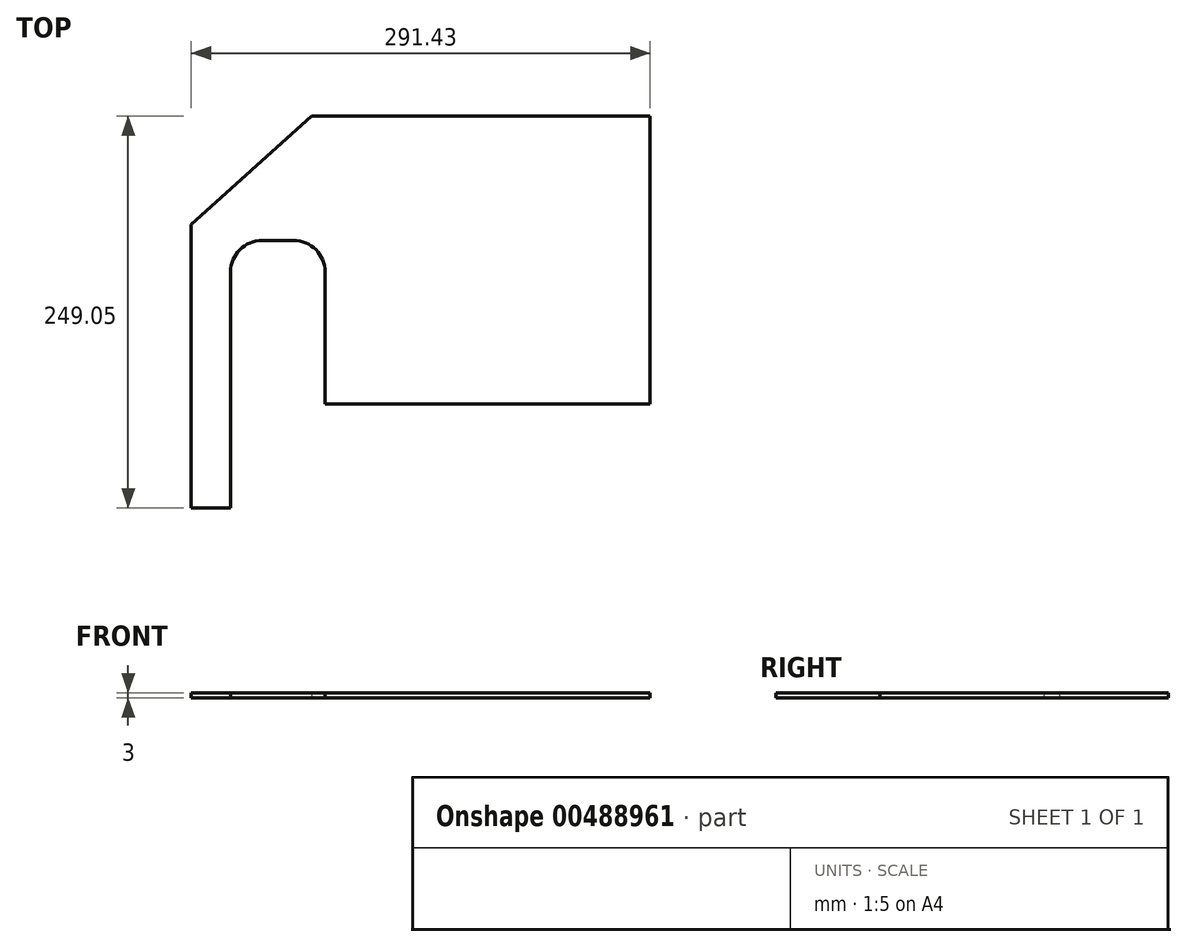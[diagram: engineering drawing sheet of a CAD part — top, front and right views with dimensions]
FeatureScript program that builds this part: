
annotation { "Feature Type Name" : "Feature", "Feature Type Description" : "" }
export const myFeature = defineFeature(function(context is Context, id is Id, definition is map)
    precondition{}
    {
        {
            var Q0;
            Q0=qCreatedBy(makeId("Top.planeOp"),FACE);
            var sketch = newSketch(context, id + "F0", { "sketchPlane" : qUnion([Q0])});
            skLineSegment(sketch, "E0", {"start": v(-110.58, 54.55) * mm, "end": v(-110.58, -125.45) * mm});
            skLineSegment(sketch, "E1", {"start": v(-110.58, -125.45) * mm, "end": v(-85.58, -125.45) * mm});
            skLineSegment(sketch, "E2", {"start": v(-85.58, -125.45) * mm, "end": v(-85.58, 24.55) * mm});
            skLineSegment(sketch, "E3", {"start": v(-65.58, 44.55) * mm, "end": v(-45.58, 44.55) * mm});
            skLineSegment(sketch, "E4", {"start": v(-25.58, 24.55) * mm, "end": v(-25.58, -59.4) * mm});
            skLineSegment(sketch, "E5", {"start": v(-25.58, -59.4) * mm, "end": v(180.85, -59.4) * mm});
            skLineSegment(sketch, "E6", {"start": v(180.85, -59.4) * mm, "end": v(180.85, 123.6) * mm});
            skLineSegment(sketch, "E7", {"start": v(180.85, 123.6) * mm, "end": v(-34.15, 123.6) * mm});
            skLineSegment(sketch, "E8", {"start": v(-34.15, 123.6) * mm, "end": v(-110.58, 54.55) * mm});
            skPoint(sketch, "E9.visualSharp", {"position": v(-85.58, 44.55) * mm});
            skArc(sketch, "E9.filletArc", {"start": v(-65.58, 44.55) * mm, "mid": v(-79.72, 38.69) * mm, "end": v(-85.58, 24.55) * mm});
            skPoint(sketch, "E10.visualSharp", {"position": v(-25.58, 44.55) * mm});
            skArc(sketch, "E10.filletArc", {"start": v(-25.58, 24.55) * mm, "mid": v(-31.43, 38.69) * mm, "end": v(-45.58, 44.55) * mm});
            skSolve(sketch);
        }
        {
            var Q0;
            Q0=makeQuery(id+"F0.imprint","IMPRINT",FACE,{"disambiguationData":[TD([[makeQuery(id+"F0.imprint","IMPRINT",EDGE,{"derivedFrom":sQuery(id+"F0.wireOp",EDGE,"E0")}),1.0]])]});
            extrude(context, id + "F1", {"entities" : qUnion([Q0]), "depth" : 3 * mm});
        }
    });
